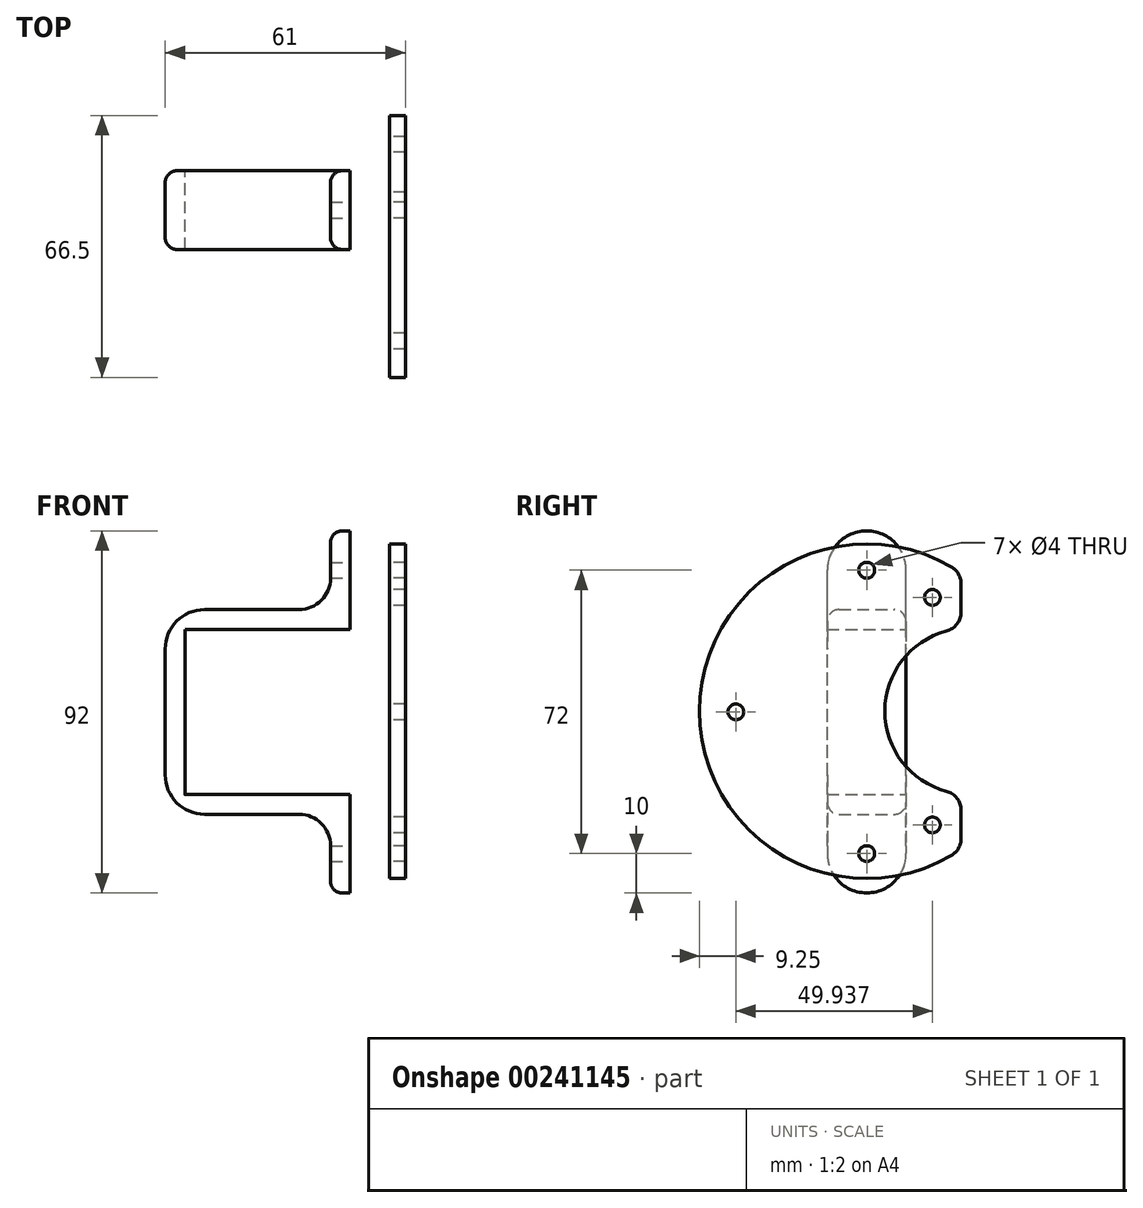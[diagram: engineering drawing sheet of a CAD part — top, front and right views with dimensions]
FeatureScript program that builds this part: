
annotation { "Feature Type Name" : "Feature", "Feature Type Description" : "" }
export const myFeature = defineFeature(function(context is Context, id is Id, definition is map)
    precondition{}
    {
        {
            var Q0;
            Q0=qCreatedBy(makeId("Front.planeOp"),FACE);
            var sketch = newSketch(context, id + "F0", { "sketchPlane" : qUnion([Q0])});
            skLineSegment(sketch, "E0.bottom", {"start": v(10, 21) * mm, "end": v(-10, 21) * mm});
            skLineSegment(sketch, "E0.top", {"start": v(10, -21) * mm, "end": v(-10, -21) * mm});
            skLineSegment(sketch, "E0.left", {"start": v(10, 21) * mm, "end": v(10, -21) * mm});
            skLineSegment(sketch, "E0.right", {"start": v(-10, 21) * mm, "end": v(-10, -21) * mm});
            skPoint(sketch, "E0.middle", {"position": v(0, 0) * mm});
            skLineSegment(sketch, "E1", {"start": v(-10, 21) * mm, "end": v(-10, 46) * mm});
            skLineSegment(sketch, "E2", {"start": v(-10, 46) * mm, "end": v(10, 46) * mm});
            skLineSegment(sketch, "E3", {"start": v(10, 46) * mm, "end": v(10, 21) * mm});
            skLineSegment(sketch, "E4", {"start": v(-10, -21) * mm, "end": v(-10, -46) * mm});
            skLineSegment(sketch, "E5", {"start": v(-10, -46) * mm, "end": v(10, -46) * mm});
            skLineSegment(sketch, "E6", {"start": v(10, -46) * mm, "end": v(10, -21) * mm});
            skCircle(sketch, "E7", {"center": v(0, 33.5) * mm, "radius": 2 * mm});
            skPoint(sketch, "E7.centerSnap0", {"position": v(-10, 33.5) * mm});
            skCircle(sketch, "E8", {"center": v(0, -33.5) * mm, "radius": 2 * mm});
            skPoint(sketch, "E8.centerSnap0", {"position": v(-10, -33.5) * mm});
            skPoint(sketch, "E8.centerSnap1", {"position": v(0, -21) * mm});
            skLineSegment(sketch, "E9", {"start": v(-10, -21) * mm, "end": v(-52, -21) * mm});
            skLineSegment(sketch, "E10", {"start": v(-52, -21) * mm, "end": v(-52, 21) * mm});
            skLineSegment(sketch, "E11", {"start": v(-52, 21) * mm, "end": v(-10, 21) * mm});
            skLineSegment(sketch, "E12.0", {"start": v(-15, -26) * mm, "end": v(-15, -46) * mm});
            skLineSegment(sketch, "E12.1", {"start": v(-15, 26) * mm, "end": v(-15, 46) * mm});
            skLineSegment(sketch, "E12.2", {"start": v(-57, 26) * mm, "end": v(-15, 26) * mm});
            skLineSegment(sketch, "E12.3", {"start": v(-57, -26) * mm, "end": v(-57, 26) * mm});
            skLineSegment(sketch, "E12.4", {"start": v(-15, -26) * mm, "end": v(-57, -26) * mm});
            skLineSegment(sketch, "E13", {"start": v(-15, -46) * mm, "end": v(-10, -46) * mm});
            skLineSegment(sketch, "E14", {"start": v(-15, 46) * mm, "end": v(-10, 46) * mm});
            skSolve(sketch);
        }
        {
            var Q0;
            Q0=makeQuery(id+"F0.imprint","IMPRINT",FACE,{"disambiguationData":[TD([[makeQuery(id+"F0.imprint","IMPRINT",EDGE,{"derivedFrom":sQuery(id+"F0.wireOp",EDGE,"E1")}),1.0]])]});
            extrude(context, id + "F1", {"entities" : qUnion([Q0]), "depth" : 20 * mm});
        }
        {
            var Q0;
            Q0=makeQuery(id+"F1.opExtrude","SWEPT_EDGE",EDGE,{"disambiguationData":[OSD([sQuery(id+"F0.wireOp",EDGE,"E12.0"),sQuery(id+"F0.wireOp",EDGE,"E12.4")])]});
            var Q1;
            Q1=makeQuery(id+"F1.opExtrude","SWEPT_EDGE",EDGE,{"disambiguationData":[OSD([sQuery(id+"F0.wireOp",EDGE,"E12.1"),sQuery(id+"F0.wireOp",EDGE,"E12.2")])]});
            fillet(context, id + "F2", {"entities" : qUnion([Q0, Q1]), "radius" : 8 * mm, "tangentPropagation" : true, "allowEdgeOverflow" : false});
        }
        {
            var Q0;
            Q0=makeQuery(id+"F1.opExtrude","CAP_EDGE",EDGE,{"disambiguationData":[OSD([sQuery(id+"F0.wireOp",EDGE,"E14")])],"isStart":true});
            var Q1;
            Q1=makeQuery(id+"F1.opExtrude","CAP_EDGE",EDGE,{"disambiguationData":[OSD([sQuery(id+"F0.wireOp",EDGE,"E14")])],"isStart":false});
            var Q2;
            Q2=makeQuery(id+"F1.opExtrude","CAP_EDGE",EDGE,{"disambiguationData":[OSD([sQuery(id+"F0.wireOp",EDGE,"E13")])],"isStart":true});
            var Q3;
            Q3=makeQuery(id+"F1.opExtrude","CAP_EDGE",EDGE,{"disambiguationData":[OSD([sQuery(id+"F0.wireOp",EDGE,"E13")])],"isStart":false});
            var Q4;
            Q4=makeQuery(id+"F1.opExtrude","SWEPT_EDGE",EDGE,{"disambiguationData":[OSD([sQuery(id+"F0.wireOp",EDGE,"E12.3"),sQuery(id+"F0.wireOp",EDGE,"E12.4")])]});
            var Q5;
            Q5=makeQuery(id+"F1.opExtrude","SWEPT_EDGE",EDGE,{"disambiguationData":[OSD([sQuery(id+"F0.wireOp",EDGE,"E12.2"),sQuery(id+"F0.wireOp",EDGE,"E12.3")])]});
            fillet(context, id + "F3", {"entities" : qUnion([Q0, Q1, Q2, Q3, Q4, Q5]), "radius" : 10 * mm, "tangentPropagation" : true, "allowEdgeOverflow" : false});
        }
        {
            var Q0;
            Q0=makeQuery(id+"F1.opExtrude","CAP_EDGE",EDGE,{"disambiguationData":[OSD([sQuery(id+"F0.wireOp",EDGE,"E12.3")])],"isStart":true});
            fillet(context, id + "F4", {"entities" : qUnion([Q0]), "radius" : 3 * mm, "tangentPropagation" : true, "allowEdgeOverflow" : false});
        }
        {
            var Q0;
            Q0=makeQuery(id+"F1.opExtrude","SWEPT_FACE",FACE,{"disambiguationData":[OSD([sQuery(id+"F0.wireOp",EDGE,"E1")])]});
            var sketch = newSketch(context, id + "F5", { "sketchPlane" : qUnion([Q0])});
            skPoint(sketch, "E15", {"position": v(-10, 36) * mm});
            skSolve(sketch);
        }
        {
            var Q0;
            Q0=makeQuery(id+"F1.opExtrude","SWEPT_FACE",FACE,{"disambiguationData":[OSD([sQuery(id+"F0.wireOp",EDGE,"E4")])]});
            var sketch = newSketch(context, id + "F6", { "sketchPlane" : qUnion([Q0])});
            skPoint(sketch, "E16", {"position": v(-10, -36) * mm});
            skSolve(sketch);
        }
        {
            var Q0;
            Q0=qCreatedBy(makeId("Right.planeOp"),FACE);
            var sketch = newSketch(context, id + "F7", { "sketchPlane" : qUnion([Q0])});
            skArc(sketch, "E17.cCircle", {"start": v(11.53, 36.83) * mm, "mid": v(-52.5, 0.19) * mm, "end": v(11.53, -36.45) * mm});
            skLineSegment(sketch, "E18", {"start": v(-34, 0) * mm, "end": v(-52.5, 0) * mm, "construction": true});
            skLineSegment(sketch, "E19", {"start": v(2.12, 21.19) * mm, "end": v(11.25, 37) * mm, "construction": true});
            skLineSegment(sketch, "E20", {"start": v(2.12, -20.81) * mm, "end": v(11.25, -36.62) * mm, "construction": true});
            skCircle(sketch, "E21", {"center": v(6.69, 29.1) * mm, "radius": 2 * mm});
            skCircle(sketch, "E22", {"center": v(6.69, -28.71) * mm, "radius": 2 * mm});
            skCircle(sketch, "E23", {"center": v(-43.25, 0) * mm, "radius": 2 * mm});
            skLineSegment(sketch, "E24", {"start": v(14, -25) * mm, "end": v(14, -32.14) * mm});
            skLineSegment(sketch, "E25", {"start": v(14, 25.39) * mm, "end": v(14, 32.52) * mm});
            skPoint(sketch, "E26.visualSharp", {"position": v(14, -34.89) * mm});
            skArc(sketch, "E26.filletArc", {"start": v(11.53, -36.45) * mm, "mid": v(13.34, -34.62) * mm, "end": v(14, -32.14) * mm});
            skPoint(sketch, "E27.visualSharp", {"position": v(14, 35.26) * mm});
            skArc(sketch, "E27.filletArc", {"start": v(14, 32.52) * mm, "mid": v(13.34, 35) * mm, "end": v(11.53, 36.83) * mm});
            skArc(sketch, "E28", {"start": v(10.28, 20.55) * mm, "mid": v(-5.4, 0.19) * mm, "end": v(10.28, -20.18) * mm});
            skPoint(sketch, "E29.visualSharp", {"position": v(14, -20.81) * mm});
            skArc(sketch, "E29.filletArc", {"start": v(14, -25) * mm, "mid": v(12.96, -21.96) * mm, "end": v(10.28, -20.18) * mm});
            skPoint(sketch, "E30.visualSharp", {"position": v(14, 21.19) * mm});
            skArc(sketch, "E30.filletArc", {"start": v(10.28, 20.55) * mm, "mid": v(12.96, 22.34) * mm, "end": v(14, 25.39) * mm});
            skSolve(sketch);
        }
        {
            var Q0;
            Q0=makeQuery(id+"F7.imprint","IMPRINT",FACE,{"disambiguationData":[TD([[makeQuery(id+"F7.imprint","IMPRINT",EDGE,{"derivedFrom":sQuery(id+"F7.wireOp",EDGE,"E17.cCircle")}),1.0]])]});
            extrude(context, id + "F8", {"entities" : qUnion([Q0]), "depth" : 4 * mm});
        }
        {
            var Q0;
            Q0=sQuery(id+"F6.wireOp",VERTEX,"E16");
            var Q1;
            Q1=sQuery(id+"F5.wireOp",VERTEX,"E15");
            var Q2;
            Q2=makeQuery(id+"F1.opExtrude","SWEPT_BODY",BODY,{"disambiguationData":[OSD([sQuery(id+"F0.wireOp",EDGE,"E1"),sQuery(id+"F0.wireOp",EDGE,"E4"),sQuery(id+"F0.wireOp",EDGE,"E9"),sQuery(id+"F0.wireOp",EDGE,"E10"),sQuery(id+"F0.wireOp",EDGE,"E11"),sQuery(id+"F0.wireOp",EDGE,"E12.0"),sQuery(id+"F0.wireOp",EDGE,"E12.1"),sQuery(id+"F0.wireOp",EDGE,"E12.2"),sQuery(id+"F0.wireOp",EDGE,"E12.3"),sQuery(id+"F0.wireOp",EDGE,"E12.4"),sQuery(id+"F0.wireOp",EDGE,"E13"),sQuery(id+"F0.wireOp",EDGE,"E14")])]});
            hole(context, id + "F9", {"style" : HoleStyle.SIMPLE, "endStyle" : HoleEndStyle.THROUGH, "holeDiameter" : 4 * mm, "locations" : qUnion([Q0, Q1]), "scope" : qUnion([Q2]), "isTappedThrough" : true});
        }
        {
            var Q0;
            Q0=sQuery(id+"F6.wireOp",VERTEX,"E16");
            var Q1;
            Q1=sQuery(id+"F5.wireOp",VERTEX,"E15");
            var Q2;
            Q2=makeQuery(id+"F8.opExtrude","SWEPT_BODY",BODY,{"disambiguationData":[OSD([sQuery(id+"F7.wireOp",EDGE,"E17.cCircle"),sQuery(id+"F7.wireOp",EDGE,"zXcFPkvp-JhwL-ozvX-gc98-i9kPBDctdqnc.right"),sQuery(id+"F7.wireOp",EDGE,"eFwaOwum-OMeb-qqHv-tQyo-3uMKuW7qRpQr"),sQuery(id+"F7.wireOp",EDGE,"uwqSzxH3-6ROS-wm4n-dcTt-mgJaT3Llr0zS"),sQuery(id+"F7.wireOp",EDGE,"E21"),sQuery(id+"F7.wireOp",EDGE,"E22"),sQuery(id+"F7.wireOp",EDGE,"E23"),sQuery(id+"F7.wireOp",EDGE,"e82546dc-71f0-4cad-9ae1-4764872d9041.filletArc"),sQuery(id+"F7.wireOp",EDGE,"f49e4d2a-3805-4f8e-a0e0-cf14b65f8dca.filletArc")])]});
            hole(context, id + "F10", {"style" : HoleStyle.SIMPLE, "endStyle" : HoleEndStyle.THROUGH, "oppositeDirection" : true, "holeDiameter" : 4 * mm, "locations" : qUnion([Q0, Q1]), "scope" : qUnion([Q2]), "isTappedThrough" : true});
        }
    });
